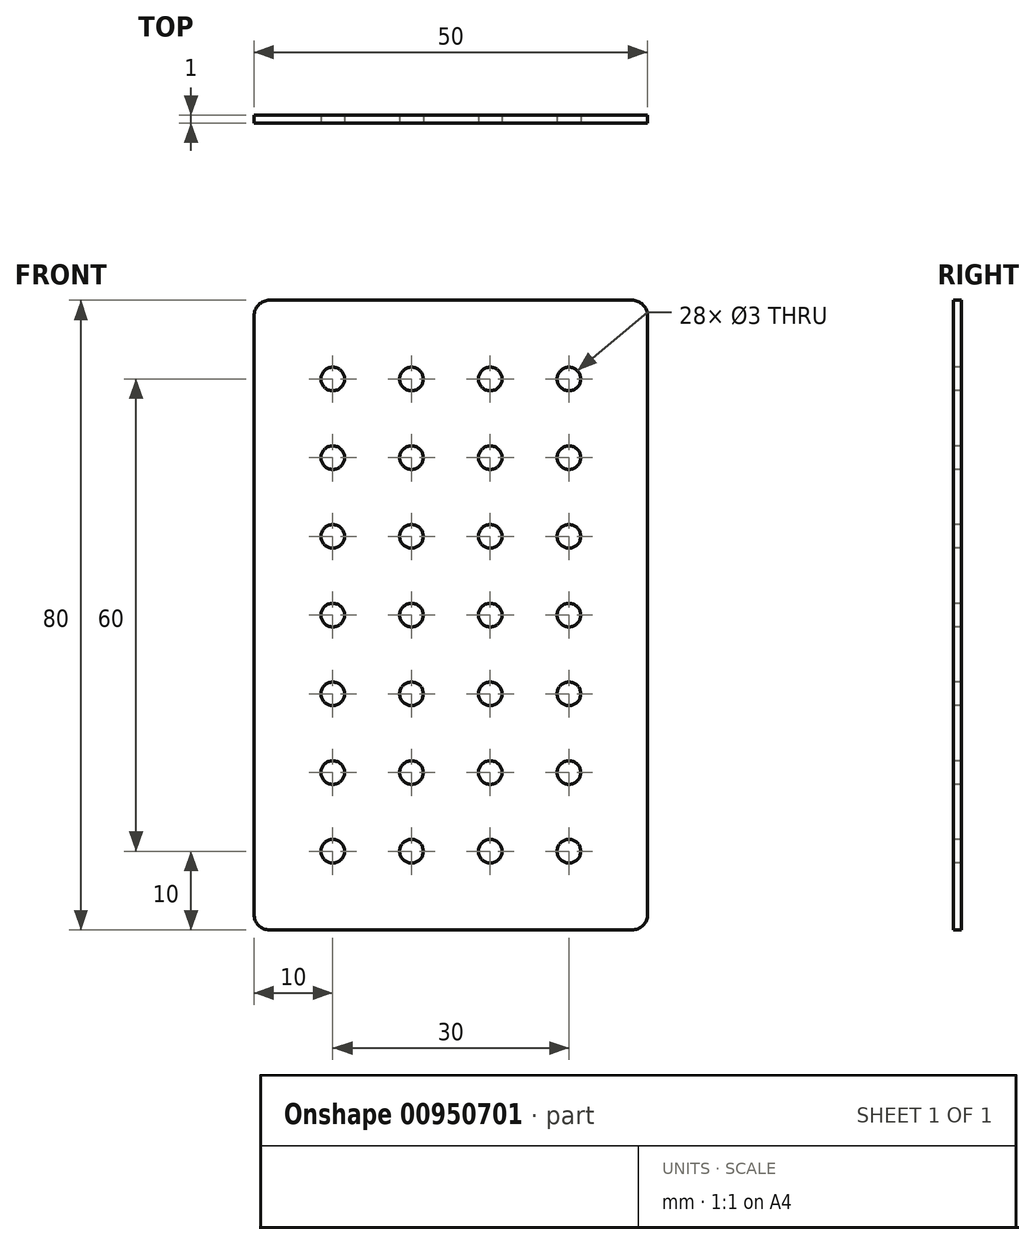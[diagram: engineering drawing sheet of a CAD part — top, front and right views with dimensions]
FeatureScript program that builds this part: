
annotation { "Feature Type Name" : "Feature", "Feature Type Description" : "" }
export const myFeature = defineFeature(function(context is Context, id is Id, definition is map)
    precondition{}
    {
        {
            var Q0;
            Q0=qCreatedBy(makeId("Front.planeOp"),FACE);
            var sketch = newSketch(context, id + "F0", { "sketchPlane" : qUnion([Q0])});
            skLineSegment(sketch, "E0.bottom", {"start": v(0, 0) * mm, "end": v(-50, 0) * mm});
            skLineSegment(sketch, "E0.top", {"start": v(0, 80) * mm, "end": v(-50, 80) * mm});
            skLineSegment(sketch, "E0.left", {"start": v(0, 0) * mm, "end": v(0, 80) * mm});
            skLineSegment(sketch, "E0.right", {"start": v(-50, 0) * mm, "end": v(-50, 80) * mm});
            skSolve(sketch);
        }
        {
            var Q0;
            Q0=makeQuery(id+"F0.imprint","IMPRINT",FACE,{"disambiguationData":[TD([[makeQuery(id+"F0.imprint","IMPRINT",EDGE,{"derivedFrom":sQuery(id+"F0.wireOp",EDGE,"E0.bottom")}),-1.0]])]});
            extrude(context, id + "F1", {"entities" : qUnion([Q0]), "depth" : 1 * mm, "offsetDistance" : 25 * mm});
        }
        {
            var Q0;
            Q0=makeQuery(id+"F1.opExtrude","CAP_FACE",FACE,{"disambiguationData":[OSD([sQuery(id+"F0.wireOp",EDGE,"E0.bottom"),sQuery(id+"F0.wireOp",EDGE,"E0.top"),sQuery(id+"F0.wireOp",EDGE,"E0.left"),sQuery(id+"F0.wireOp",EDGE,"E0.right")])],"isStart":false});
            var sketch = newSketch(context, id + "F2", { "sketchPlane" : qUnion([Q0])});
            skLineSegment(sketch, "E1.direction1", {"start": v(-50, 0) * mm, "end": v(-40, 0) * mm, "construction": true});
            skCircle(sketch, "E2", {"center": v(-40, 70) * mm, "radius": 1.5 * mm});
            skCircle(sketch, "E3", {"center": v(-30, 70) * mm, "radius": 1.5 * mm});
            skCircle(sketch, "E4", {"center": v(-20, 70) * mm, "radius": 1.5 * mm});
            skCircle(sketch, "E5", {"center": v(-10, 70) * mm, "radius": 1.5 * mm});
            skCircle(sketch, "E6", {"center": v(-40, 60) * mm, "radius": 1.5 * mm});
            skCircle(sketch, "E7", {"center": v(-30, 60) * mm, "radius": 1.5 * mm});
            skCircle(sketch, "E8", {"center": v(-20, 60) * mm, "radius": 1.5 * mm});
            skCircle(sketch, "E9", {"center": v(-10, 60) * mm, "radius": 1.5 * mm});
            skCircle(sketch, "E10", {"center": v(-40, 50) * mm, "radius": 1.5 * mm});
            skCircle(sketch, "E11", {"center": v(-30, 50) * mm, "radius": 1.5 * mm});
            skCircle(sketch, "E12", {"center": v(-20, 50) * mm, "radius": 1.5 * mm});
            skCircle(sketch, "E13", {"center": v(-10, 50) * mm, "radius": 1.5 * mm});
            skCircle(sketch, "E14", {"center": v(-40, 40) * mm, "radius": 1.5 * mm});
            skCircle(sketch, "E15", {"center": v(-30, 40) * mm, "radius": 1.5 * mm});
            skCircle(sketch, "E16", {"center": v(-20, 40) * mm, "radius": 1.5 * mm});
            skCircle(sketch, "E17", {"center": v(-10, 40) * mm, "radius": 1.5 * mm});
            skCircle(sketch, "E18", {"center": v(-40, 30) * mm, "radius": 1.5 * mm});
            skCircle(sketch, "E19", {"center": v(-30, 30) * mm, "radius": 1.5 * mm});
            skCircle(sketch, "E20", {"center": v(-20, 30) * mm, "radius": 1.5 * mm});
            skCircle(sketch, "E21", {"center": v(-10, 30) * mm, "radius": 1.5 * mm});
            skCircle(sketch, "E22", {"center": v(-40, 20) * mm, "radius": 1.5 * mm});
            skCircle(sketch, "E23", {"center": v(-30, 20) * mm, "radius": 1.5 * mm});
            skCircle(sketch, "E24", {"center": v(-20, 20) * mm, "radius": 1.5 * mm});
            skCircle(sketch, "E25", {"center": v(-10, 20) * mm, "radius": 1.5 * mm});
            skCircle(sketch, "E26", {"center": v(-40, 10) * mm, "radius": 1.5 * mm});
            skCircle(sketch, "E27", {"center": v(-30, 10) * mm, "radius": 1.5 * mm});
            skCircle(sketch, "E28", {"center": v(-20, 10) * mm, "radius": 1.5 * mm});
            skCircle(sketch, "E29", {"center": v(-10, 10) * mm, "radius": 1.5 * mm});
            skSolve(sketch);
        }
        {
            var Q0;
            Q0 = qSketchRegion(id + "F2", true);
            extrude(context, id + "F3", {"entities" : qUnion([Q0]), "operationType" : NewBodyOperationType.REMOVE, "oppositeDirection" : true, "depth" : 25 * mm, "offsetDistance" : 25 * mm});
        }
        {
            var Q0;
            Q0=makeQuery(id+"F1.opExtrude","SWEPT_EDGE",EDGE,{"disambiguationData":[OSD([sQuery(id+"F0.wireOp",EDGE,"E0.bottom"),sQuery(id+"F0.wireOp",EDGE,"E0.left")])]});
            var Q1;
            Q1=makeQuery(id+"F1.opExtrude","SWEPT_EDGE",EDGE,{"disambiguationData":[OSD([sQuery(id+"F0.wireOp",EDGE,"E0.top"),sQuery(id+"F0.wireOp",EDGE,"E0.left")])]});
            var Q2;
            Q2=makeQuery(id+"F1.opExtrude","SWEPT_EDGE",EDGE,{"disambiguationData":[OSD([sQuery(id+"F0.wireOp",EDGE,"E0.top"),sQuery(id+"F0.wireOp",EDGE,"E0.right")])]});
            var Q3;
            Q3=makeQuery(id+"F1.opExtrude","SWEPT_EDGE",EDGE,{"disambiguationData":[OSD([sQuery(id+"F0.wireOp",EDGE,"E0.bottom"),sQuery(id+"F0.wireOp",EDGE,"E0.right")])]});
            fillet(context, id + "F4", {"entities" : qUnion([Q0, Q1, Q2, Q3]), "radius" : 2 * mm, "tangentPropagation" : true, "allowEdgeOverflow" : false});
        }
    });
